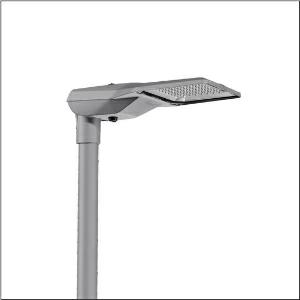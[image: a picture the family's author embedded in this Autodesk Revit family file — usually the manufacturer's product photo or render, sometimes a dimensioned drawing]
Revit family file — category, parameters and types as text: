
# Revit family: streetlight_sl_21_midi___st0_5a_5xe3b33t08mb_6d0d
name_source: partatom
category: Lighting Fixtures
units: mm (PartAtom-declared; Revit-internal decimal feet)

## family parameters
Cut with Voids When Loaded = No
Host = Face
Light Source = No
Part Type = Normal
Room Calculation Point = No
Round Connector Dimension = Use Diameter
Shared = No

## types (1)
- --- (1 x LED, 18270 lm, 136 W, 3000K)
    Apparent Load = 136 VA
    CIE Flux Codes = 41 75 97 100 100
    Color Rendering = 70
    Color Temperature = 3000K
    Default Elevation = 1800 mm
    Description = Streetlight SL 21 midi, mast luminaire, primary light control with lens, of PMMA, primary optical cover: cover, of toughened safety glass, transparent, light distribution: ST0.5a, light emission: direct distribution, primary light characteristic: asymmetric, installation type: side-entry, post-top, LED, High Power LED, rated luminous flux: 18.270lm, luminous efficacy: 134lm/W, light colour: 730, colour temperature: 3000K, control: overheat protection, constant luminous flux control, time-dependent luminous flux control, flexible luminous flux parameterisation, presetting dimming logarithmic, mains connection: 230..240V, AC, 50/60Hz, start of lifetime: 136W, end of service life: 142W, reduction: 61W, luminaire housing, of diecast aluminium, powder-coated, Siteco® metallic grey (DB 702S), corrosivity category C5 mid according to DIN EN ISO 12944, please order mast flange separately, inclination adjustable: 0°, 5°, 10°, 15°, sealing non-destructively replaceable, multi-level sealing system, length: 644mm, width: 335mm, height: 110mm, mast flange for spigot size: 42mm (side-entry): 5XC10008XM4, 60/48mm (side-entry/post-top): 5XC10108XM2, 76/60mm (side-entry/post-top): 5XC10108XM1, Smart Interface below and above, protection rating (complete): IP66, insulation class (complete): insulation class II (safety insulation), certification: CE, ENEC, ENEC+, VDE, impact resistance: IK09, permissible operating ambient temperature for outdoor applications: -40..+50°C, standard-compliant lighting for roads and squares, packaging unit: 1 piece

Light Distribution: ST0.5a
    Height = 111 mm
    Lamp = 1 x LED
    Lamp Light Flux = 18270 lm
    Lamp Power = 136 W
    Lamp count = 1
    Length = 644 mm
    Luminous efficacy = 134 lm/W
    Manufacturer = Siteco
    ModVariant = No
    Model = 5XE3B33T08MB
    Number of Poles = 1
    OnlyDefault = Yes
    Power Factor = 1
    Product Name = Streetlight SL 21 midi | ST0.5a
    Product group = mast luminaire | pylon top
    ProductGroupID = 6100
    Protection Class = Protection class II
    Protection Degree = IP 66
    RLX_Detail_Level = 1
    RLX_Emergency_Light_Flux = 0 lm
    RLX_Emergency_Type = 0
    RLX_Emergency_Type_DB = No
    RlxData = <blob elided: 101965 chars, md5=9fe893ed>
    Socket = socket
    Standby Power = 0 W
    System Light Flux = 18270 lm
    System Power = 136 W
    Type Comments = factory setting: luminous flux: 100 % | dim-lin: 254 | 695 mA
    Type Image = l_1004304.jpg
    URL = http://relux.com
    VarID = @adj_125789
    Voltage = 0 V
    Weight = 0.00 kg
    Width = 336 mm

## geometry (parser evidence)
native form markers: Blend x4, Sweep x10
no freeform markers — native parametric forms only
